# Revit family: Skylight_Architectural_ArtisticSkylight_MW-CF-FF-VE
name_source: partatom
category: Windows
units: mm (PartAtom-declared; Revit-internal decimal feet)

## family parameters
Classification Number = 23.30.30.17.24
Cut with Voids When Loaded = No
Host = Face
Room Calculation Point = No
Shared = No

## types (7) — shared parameters
Air Infiltration = 0.06 cfm
Assembly Code = B3020110
Construction Details = http://arcat.com
Curb Thickness = 0' - 3 1/2"
Default Elevation = 0' - 0"
Green Building-LEED = http://arcat.com
Keynote = 8600
Manufacturer = Artistic Skylight Domes Ltd.
Manufacturer Fax = 416-747-6630
Manufacturer Website = http://artisticskylight.com
Product Data = http://arcat.com
Revision = R1_02_2014
Sales Information = http://artisticskylight.com
Send Message = http://arcat.com
Specification = http://arcat.com
Standards Conformance = Class A Type 2 or Type 3
Structural Test Pressure = Glazing +/- 60 psf
Test Data = http://artisticskylight.com
URL = http://artisticskylight.com
Water Penetration = No Penetration at 12 psf
zero-valued in all types: Expected Lifespan (Years), Maintenance Schedule (Months), Warranty Duration (Years)

## per-type parameters (varying)
| type | Description | Height | Model | Rough Height |
| 96 x Unlimited | Artistic Skylights Fixed Continuous Skylight - Architectural Dome Model MW-CF-FF-VE - 96 | 7' - 8 1/2" | MW-CF-FF-VE - 96 | 7' - 1 1/2" |
| 80 x Unlimited | Artistic Skylights Fixed Continuous Skylight - Architectural Dome Model MW-CF-FF-VE - 80 | 6' - 6" | MW-CF-FF-VE - 80 | 5' - 11" |
| 72 x Unlimited | Artistic Skylights Fixed Continuous Skylight - Architectural Dome Model MW-CF-FF-VE - 72 | 5' - 10" | MW-CF-FF-VE - 72 | 5' - 3" |
| 60 x Unlimited | Artistic Skylights Fixed Continuous Skylight - Architectural Dome Model MW-CF-FF-VE - 60 | 4' - 10" | MW-CF-FF-VE - 60 | 4' - 3" |
| 52 x Unlimited | Artistic Skylights Fixed Continuous Skylight - Architectural Dome Model MW-CF-FF-VE - 52 | 4' - 1 1/4" | MW-CF-FF-VE - 52 | 3' - 6 1/4" |
| 42 x Unlimited | Artistic Skylights Fixed Continuous Skylight - Architectural Dome Model MW-CF-FF-VE - 42 | 3' - 4" | MW-CF-FF-VE - 42 | 2' - 9" |
| 36 x Unlimited | Artistic Skylights Fixed Continuous Skylight - Architectural Dome Model MW-CF-FF-VE - 36 | 2' - 9 1/4" | MW-CF-FF-VE - 36 | 2' - 2 1/4" |

## geometry (parser evidence)
native form markers: Blend x6, Sweep x6
no freeform markers — native parametric forms only
